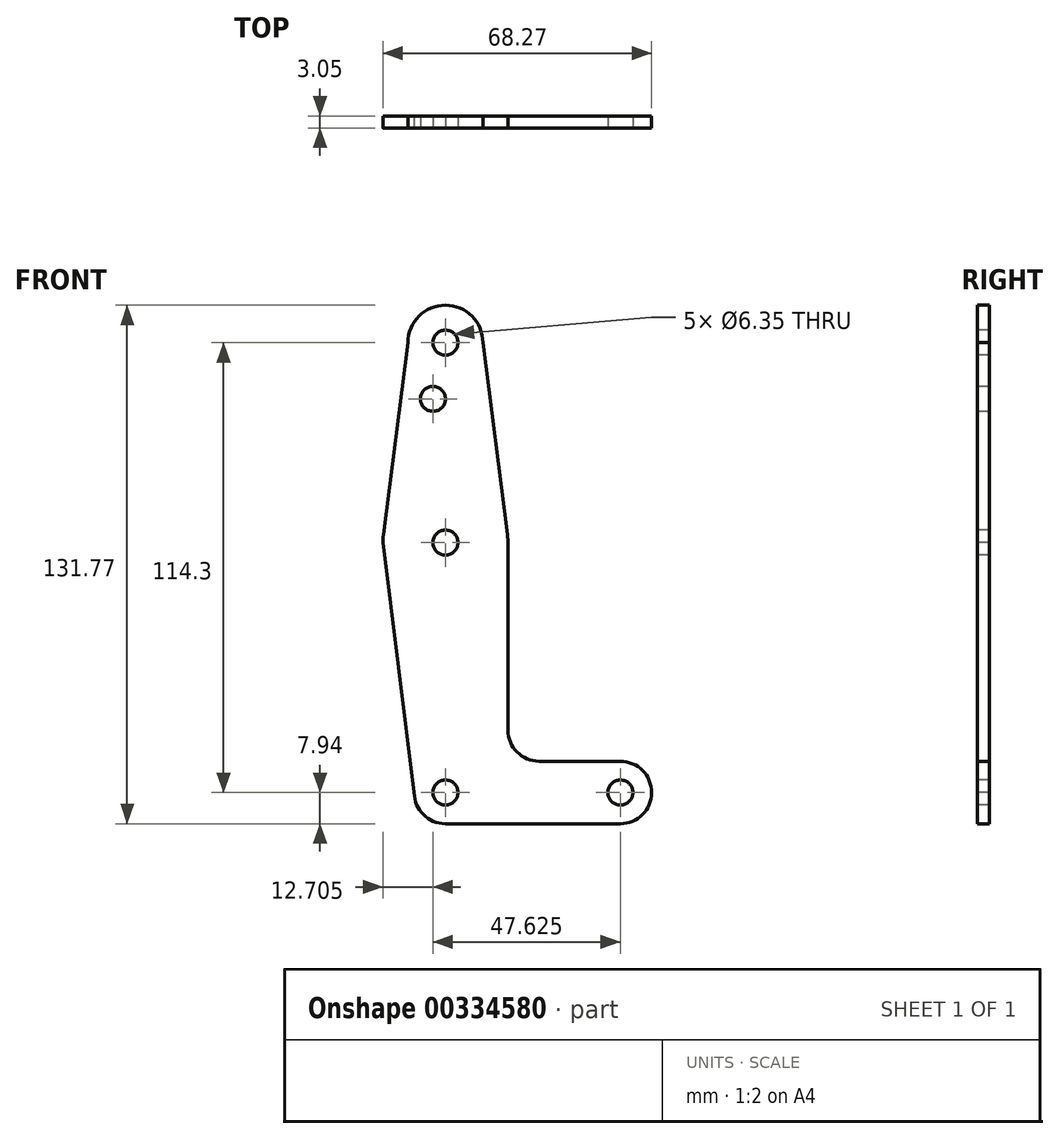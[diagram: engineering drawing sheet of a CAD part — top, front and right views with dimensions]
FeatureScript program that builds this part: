
annotation { "Feature Type Name" : "Feature", "Feature Type Description" : "" }
export const myFeature = defineFeature(function(context is Context, id is Id, definition is map)
    precondition{}
    {
        {
            var Q0;
            Q0=qCreatedBy(makeId("Front.planeOp"),FACE);
            var sketch = newSketch(context, id + "F0", { "sketchPlane" : qUnion([Q0])});
            skLineSegment(sketch, "E0", {"start": v(0, 0) * mm, "end": v(0, 114.3) * mm, "construction": true});
            skLineSegment(sketch, "E1", {"start": v(0, 0) * mm, "end": v(44.45, 0) * mm, "construction": true});
            skCircle(sketch, "E2", {"center": v(0, 63.5) * mm, "radius": 15.88 * mm});
            skCircle(sketch, "E3", {"center": v(44.45, 0) * mm, "radius": 7.94 * mm});
            skCircle(sketch, "E4", {"center": v(0, 0) * mm, "radius": 7.94 * mm});
            skCircle(sketch, "E5", {"center": v(0, 114.3) * mm, "radius": 9.53 * mm});
            skLineSegment(sketch, "E6", {"start": v(23.83, 7.94) * mm, "end": v(44.45, 7.94) * mm});
            skLineSegment(sketch, "E7", {"start": v(0, -7.94) * mm, "end": v(44.45, -7.94) * mm});
            skLineSegment(sketch, "E8", {"start": v(9.53, 114.3) * mm, "end": v(15.75, 65.5) * mm});
            skLineSegment(sketch, "E9", {"start": v(-9.53, 114.3) * mm, "end": v(-15.75, 65.5) * mm});
            skLineSegment(sketch, "E10", {"start": v(-15.88, 63.5) * mm, "end": v(-7.94, 0) * mm});
            skLineSegment(sketch, "E11", {"start": v(15.88, 63.5) * mm, "end": v(15.88, 15.89) * mm});
            skCircle(sketch, "E12", {"center": v(0, 114.3) * mm, "radius": 3.18 * mm});
            skCircle(sketch, "E13", {"center": v(0, 0) * mm, "radius": 3.18 * mm});
            skCircle(sketch, "E14", {"center": v(44.45, 0) * mm, "radius": 3.18 * mm});
            skCircle(sketch, "E15", {"center": v(0, 63.5) * mm, "radius": 3.18 * mm});
            skArc(sketch, "E16.filletArc", {"start": v(15.88, 15.89) * mm, "mid": v(18.2, 10.27) * mm, "end": v(23.83, 7.94) * mm});
            skCircle(sketch, "E17", {"center": v(-3.18, 100.03) * mm, "radius": 3.18 * mm});
            skSolve(sketch);
        }
        {
            var Q0;
            Q0=makeQuery(id+"F0.imprint","IMPRINT",FACE,{"disambiguationData":[TD([[makeQuery(id+"F0.imprint","IMPRINT",EDGE,{"derivedFrom":sQuery(id+"F0.wireOp",EDGE,"E12")}),-1.0]])]});
            var Q1;
            {var subQ0=sQuery(id+"F0.wireOp",EDGE,"E8");Q1=makeQuery(id+"F0.imprint","IMPRINT",FACE,{"disambiguationData":[TD([[makeQuery(id+"F0.imprint","IMPRINT",EDGE,{"derivedFrom":subQ0}),-1.0]])]});}
            var Q2;
            Q2=makeQuery(id+"F0.imprint","IMPRINT",FACE,{"disambiguationData":[TD([[makeQuery(id+"F0.imprint","IMPRINT",EDGE,{"derivedFrom":sQuery(id+"F0.wireOp",EDGE,"E15")}),-1.0]])]});
            var Q3;
            {var subQ0=sQuery(id+"F0.wireOp",EDGE,"E6");Q3=makeQuery(id+"F0.imprint","IMPRINT",FACE,{"disambiguationData":[TD([[makeQuery(id+"F0.imprint","IMPRINT",EDGE,{"derivedFrom":subQ0}),-1.0]])]});}
            var Q4;
            Q4=makeQuery(id+"F0.imprint","IMPRINT",FACE,{"disambiguationData":[TD([[makeQuery(id+"F0.imprint","IMPRINT",EDGE,{"derivedFrom":sQuery(id+"F0.wireOp",EDGE,"E13")}),-1.0]])]});
            var Q5;
            Q5=makeQuery(id+"F0.imprint","IMPRINT",FACE,{"disambiguationData":[TD([[makeQuery(id+"F0.imprint","IMPRINT",EDGE,{"derivedFrom":sQuery(id+"F0.wireOp",EDGE,"E14")}),-1.0]])]});
            extrude(context, id + "F1", {"entities" : qUnion([Q0, Q1, Q2, Q3, Q4, Q5]), "oppositeDirection" : true, "depth" : 3.05 * mm});
        }
    });
